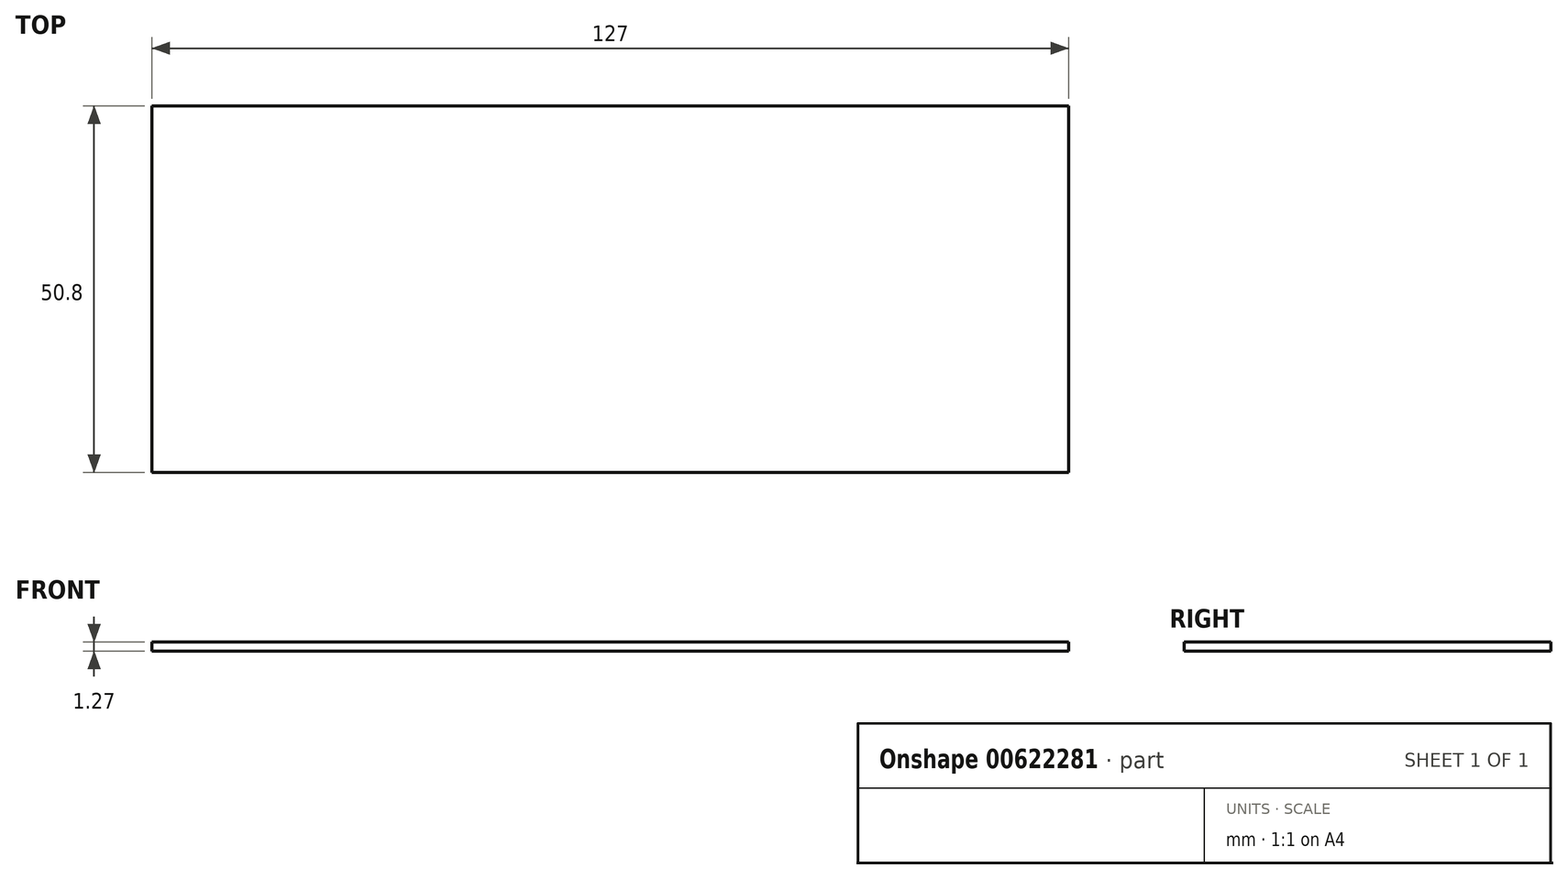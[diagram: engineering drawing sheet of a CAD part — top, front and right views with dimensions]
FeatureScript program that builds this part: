
annotation { "Feature Type Name" : "Feature", "Feature Type Description" : "" }
export const myFeature = defineFeature(function(context is Context, id is Id, definition is map)
    precondition{}
    {
        {
            var Q0;
            Q0=qCreatedBy(makeId("Top.planeOp"),FACE);
            var sketch = newSketch(context, id + "F0", { "sketchPlane" : qUnion([Q0])});
            skLineSegment(sketch, "E0", {"start": v(0, 0) * mm, "end": v(-63.5, 0) * mm});
            skLineSegment(sketch, "E1", {"start": v(-63.5, 0) * mm, "end": v(-63.5, 25.4) * mm});
            skLineSegment(sketch, "E2", {"start": v(-63.5, 25.4) * mm, "end": v(63.5, 25.4) * mm});
            skLineSegment(sketch, "E3", {"start": v(63.5, 25.4) * mm, "end": v(63.5, -25.4) * mm});
            skLineSegment(sketch, "E4", {"start": v(63.5, -25.4) * mm, "end": v(-63.5, -25.4) * mm});
            skLineSegment(sketch, "E5", {"start": v(-63.5, -25.4) * mm, "end": v(-63.5, 0) * mm});
            skSolve(sketch);
        }
        {
            var Q0;
            Q0 = qSketchRegion(id + "F0", true);
            extrude(context, id + "F1", {"entities" : qUnion([Q0]), "depth" : 1.27 * mm, "offsetDistance" : 25.4 * mm});
        }
    });
